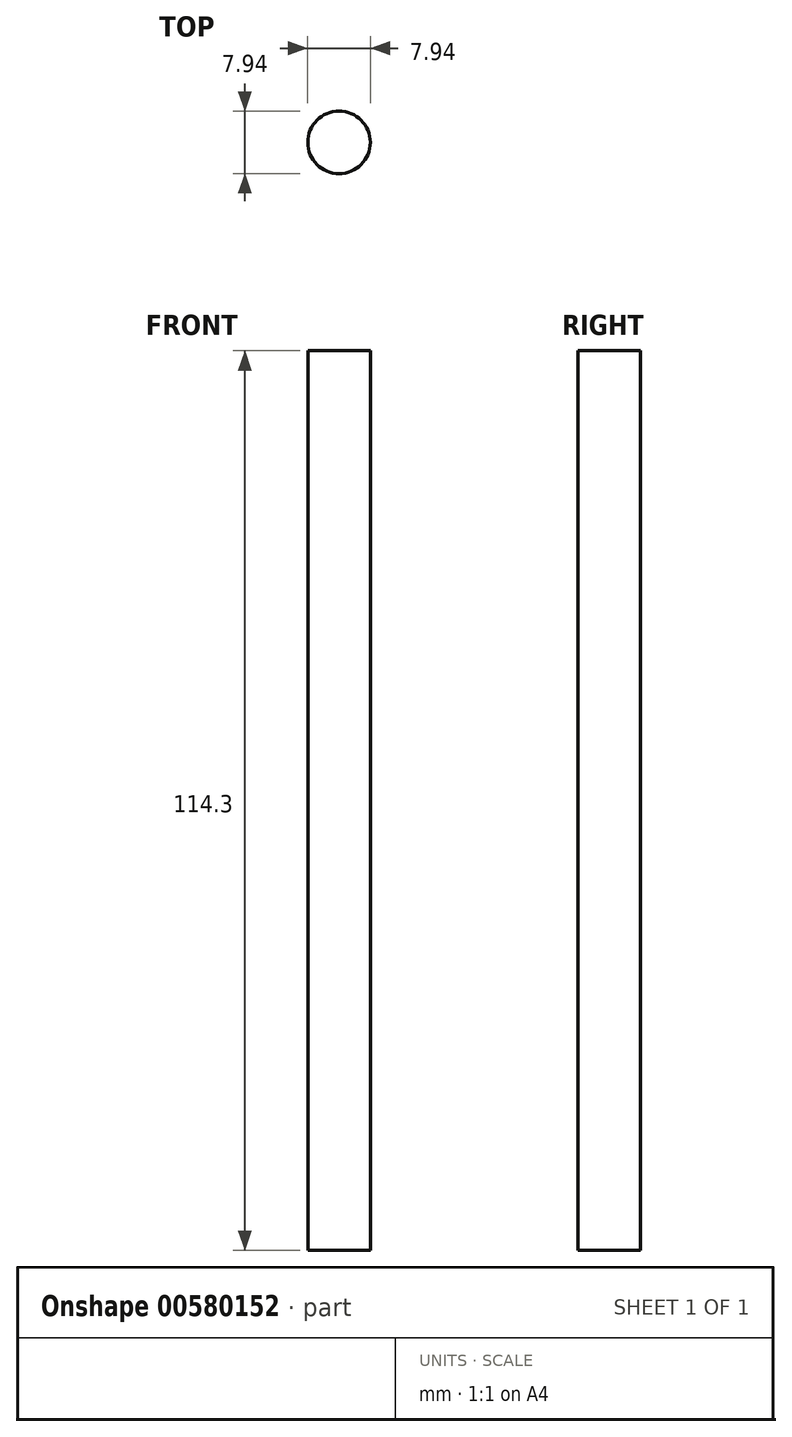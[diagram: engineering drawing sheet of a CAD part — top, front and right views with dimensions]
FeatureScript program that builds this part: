
annotation { "Feature Type Name" : "Feature", "Feature Type Description" : "" }
export const myFeature = defineFeature(function(context is Context, id is Id, definition is map)
    precondition{}
    {
        {
            var Q0;
            Q0=qCreatedBy(makeId("Top.planeOp"),FACE);
            var sketch = newSketch(context, id + "F0", { "sketchPlane" : qUnion([Q0])});
            skCircle(sketch, "E0", {"center": v(0, 0) * mm, "radius": 3.97 * mm});
            skSolve(sketch);
        }
        {
            var Q0;
            Q0=qSketchRegion(id+"F0",true);
            extrude(context, id + "F1", {"entities" : qUnion([Q0]), "depth" : 114.3 * mm});
        }
    });
